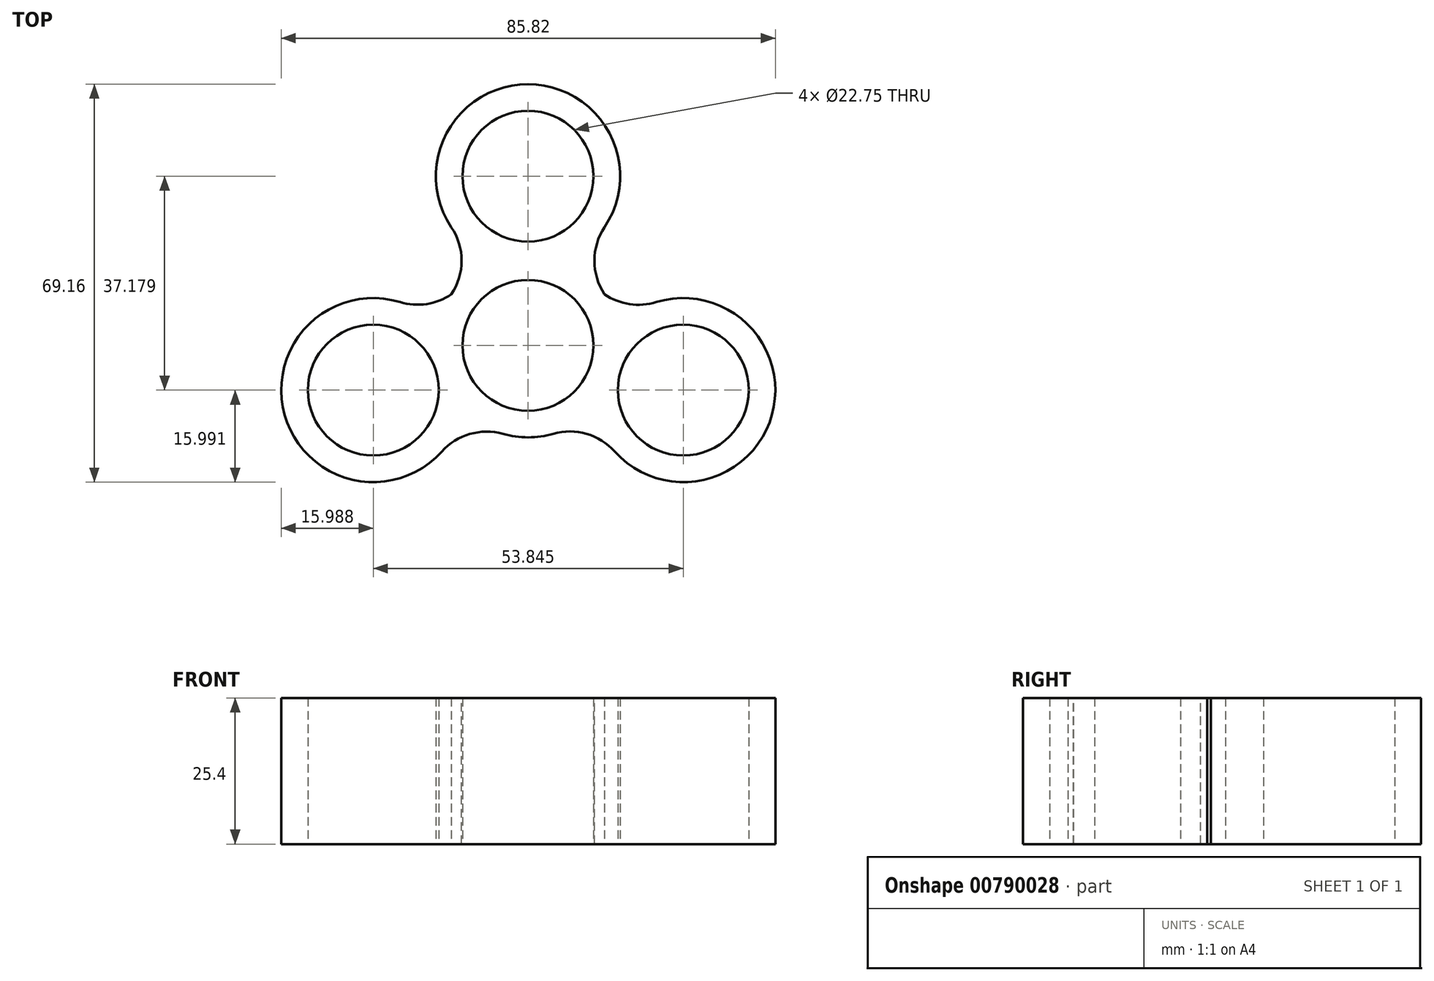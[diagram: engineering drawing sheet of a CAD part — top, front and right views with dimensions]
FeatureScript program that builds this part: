
annotation { "Feature Type Name" : "Feature", "Feature Type Description" : "" }
export const myFeature = defineFeature(function(context is Context, id is Id, definition is map)
    precondition{}
    {
        {
            var Q0;
            Q0=qCreatedBy(makeId("Top.planeOp"),FACE);
            var sketch = newSketch(context, id + "F0", { "sketchPlane" : qUnion([Q0])});
            skCircle(sketch, "E0", {"center": v(0, 29.4) * mm, "radius": 15.99 * mm});
            skCircle(sketch, "E1", {"center": v(0, 29.4) * mm, "radius": 11.37 * mm});
            skCircle(sketch, "E2", {"center": v(-26.87, -7.78) * mm, "radius": 15.99 * mm});
            skCircle(sketch, "E3", {"center": v(-26.87, -7.78) * mm, "radius": 11.37 * mm});
            skCircle(sketch, "E4", {"center": v(26.97, -7.78) * mm, "radius": 15.99 * mm});
            skCircle(sketch, "E5", {"center": v(26.97, -7.78) * mm, "radius": 11.37 * mm});
            skCircle(sketch, "E6", {"center": v(0, 0) * mm, "radius": 15.99 * mm});
            skCircle(sketch, "E7", {"center": v(0, 0) * mm, "radius": 11.37 * mm});
            skSolve(sketch);
        }
        {
            var Q0;
            Q0=makeQuery(id+"F0.imprint","IMPRINT",FACE,{"disambiguationData":[TD([[makeQuery(id+"F0.imprint","IMPRINT",EDGE,{"derivedFrom":sQuery(id+"F0.wireOp",EDGE,"E1")}),-1.0]])]});
            var Q1;
            Q1=makeQuery(id+"F0.imprint","IMPRINT",FACE,{"disambiguationData":[TD([[makeQuery(id+"F0.imprint","IMPRINT",EDGE,{"derivedFrom":sQuery(id+"F0.wireOp",EDGE,"E7")}),-1.0]])]});
            var Q2;
            Q2=makeQuery(id+"F0.imprint","IMPRINT",FACE,{"disambiguationData":[TD([[makeQuery(id+"F0.imprint","IMPRINT",EDGE,{"derivedFrom":sQuery(id+"F0.wireOp",EDGE,"E5")}),-1.0]])]});
            var Q3;
            Q3=makeQuery(id+"F0.imprint","IMPRINT",FACE,{"disambiguationData":[TD([[makeQuery(id+"F0.imprint","IMPRINT",EDGE,{"derivedFrom":sQuery(id+"F0.wireOp",EDGE,"E3")}),-1.0]])]});
            var Q4;
            {var subQ0=sQuery(id+"F0.wireOp",EDGE,"E6");var subQ1=sQuery(id+"F0.wireOp",EDGE,"E2");var subQ2=makeQuery(id+"F0.imprint","INTERSECT",VERTEX,{"disambiguationData":[OD(0.0)],"derivedFrom":[subQ1,subQ0]});Q4=makeQuery(id+"F0.imprint","IMPRINT",FACE,{"disambiguationData":[TD([[makeQuery(id+"F0.imprint","IMPRINT",EDGE,{"disambiguationData":[TD([[subQ2,1.0]])],"derivedFrom":subQ1}),1.0]])]});}
            var Q5;
            {var subQ0=sQuery(id+"F0.wireOp",EDGE,"E6");var subQ1=sQuery(id+"F0.wireOp",EDGE,"E0");var subQ2=makeQuery(id+"F0.imprint","INTERSECT",VERTEX,{"disambiguationData":[OD(0.0)],"derivedFrom":[subQ1,subQ0]});Q5=makeQuery(id+"F0.imprint","IMPRINT",FACE,{"disambiguationData":[TD([[makeQuery(id+"F0.imprint","IMPRINT",EDGE,{"disambiguationData":[TD([[subQ2,1.0]])],"derivedFrom":subQ1}),1.0]])]});}
            var Q6;
            {var subQ0=sQuery(id+"F0.wireOp",EDGE,"E6");var subQ1=sQuery(id+"F0.wireOp",EDGE,"E4");var subQ2=makeQuery(id+"F0.imprint","INTERSECT",VERTEX,{"disambiguationData":[OD(0.0)],"derivedFrom":[subQ1,subQ0]});Q6=makeQuery(id+"F0.imprint","IMPRINT",FACE,{"disambiguationData":[TD([[makeQuery(id+"F0.imprint","IMPRINT",EDGE,{"disambiguationData":[TD([[subQ2,-1.0]])],"derivedFrom":subQ1}),1.0]])]});}
            extrude(context, id + "F1", {"entities" : qUnion([Q0, Q1, Q2, Q3, Q4, Q5, Q6]), "depth" : 25.4 * mm, "offsetDistance" : 25.4 * mm});
        }
        {
            var Q0;
            {var subQ0=sQuery(id+"F0.wireOp",EDGE,"E6");var subQ1=sQuery(id+"F0.wireOp",EDGE,"E2");Q0=makeQuery(id+"F1.opExtrude","SWEPT_EDGE",EDGE,{"disambiguationData":[OSD([subQ1,subQ0]),TDD([makeQuery(id+"F0.imprint","INTERSECT",VERTEX,{"disambiguationData":[OD(1.0)],"derivedFrom":[subQ1,subQ0]})])]});}
            fillet(context, id + "F2", {"entities" : qUnion([Q0]), "radius" : 10.5 * mm, "tangentPropagation" : true, "allowEdgeOverflow" : false});
        }
        {
            var Q0;
            {var subQ0=sQuery(id+"F0.wireOp",EDGE,"E6");var subQ1=sQuery(id+"F0.wireOp",EDGE,"E0");Q0=makeQuery(id+"F1.opExtrude","SWEPT_EDGE",EDGE,{"disambiguationData":[OSD([subQ1,subQ0]),TDD([makeQuery(id+"F0.imprint","INTERSECT",VERTEX,{"disambiguationData":[OD(0.0)],"derivedFrom":[subQ1,subQ0]})])]});}
            fillet(context, id + "F3", {"entities" : qUnion([Q0]), "radius" : 10.5 * mm, "tangentPropagation" : true, "allowEdgeOverflow" : false});
        }
        {
            var Q0;
            {var subQ0=sQuery(id+"F0.wireOp",EDGE,"E6");var subQ1=sQuery(id+"F0.wireOp",EDGE,"E4");Q0=makeQuery(id+"F1.opExtrude","SWEPT_EDGE",EDGE,{"disambiguationData":[OSD([subQ1,subQ0]),TDD([makeQuery(id+"F0.imprint","INTERSECT",VERTEX,{"disambiguationData":[OD(1.0)],"derivedFrom":[subQ1,subQ0]})])]});}
            fillet(context, id + "F4", {"entities" : qUnion([Q0]), "radius" : 10.5 * mm, "tangentPropagation" : true, "allowEdgeOverflow" : false});
        }
        {
            var Q0;
            {var subQ0=sQuery(id+"F0.wireOp",EDGE,"E6");var subQ1=sQuery(id+"F0.wireOp",EDGE,"E4");Q0=makeQuery(id+"F1.opExtrude","SWEPT_EDGE",EDGE,{"disambiguationData":[OSD([subQ1,subQ0]),TDD([makeQuery(id+"F0.imprint","INTERSECT",VERTEX,{"disambiguationData":[OD(0.0)],"derivedFrom":[subQ1,subQ0]})])]});}
            fillet(context, id + "F5", {"entities" : qUnion([Q0]), "radius" : 10.5 * mm, "tangentPropagation" : true, "allowEdgeOverflow" : false});
        }
        {
            var Q0;
            {var subQ0=sQuery(id+"F0.wireOp",EDGE,"E6");var subQ1=sQuery(id+"F0.wireOp",EDGE,"E0");Q0=makeQuery(id+"F1.opExtrude","SWEPT_EDGE",EDGE,{"disambiguationData":[OSD([subQ1,subQ0]),TDD([makeQuery(id+"F0.imprint","INTERSECT",VERTEX,{"disambiguationData":[OD(1.0)],"derivedFrom":[subQ1,subQ0]})])]});}
            fillet(context, id + "F6", {"entities" : qUnion([Q0]), "radius" : 10.5 * mm, "tangentPropagation" : true, "allowEdgeOverflow" : false});
        }
        {
            var Q0;
            {var subQ0=sQuery(id+"F0.wireOp",EDGE,"E6");var subQ1=sQuery(id+"F0.wireOp",EDGE,"E2");Q0=makeQuery(id+"F1.opExtrude","SWEPT_EDGE",EDGE,{"disambiguationData":[OSD([subQ1,subQ0]),TDD([makeQuery(id+"F0.imprint","INTERSECT",VERTEX,{"disambiguationData":[OD(0.0)],"derivedFrom":[subQ1,subQ0]})])]});}
            fillet(context, id + "F7", {"entities" : qUnion([Q0]), "radius" : 10.5 * mm, "tangentPropagation" : true, "allowEdgeOverflow" : false});
        }
    });
